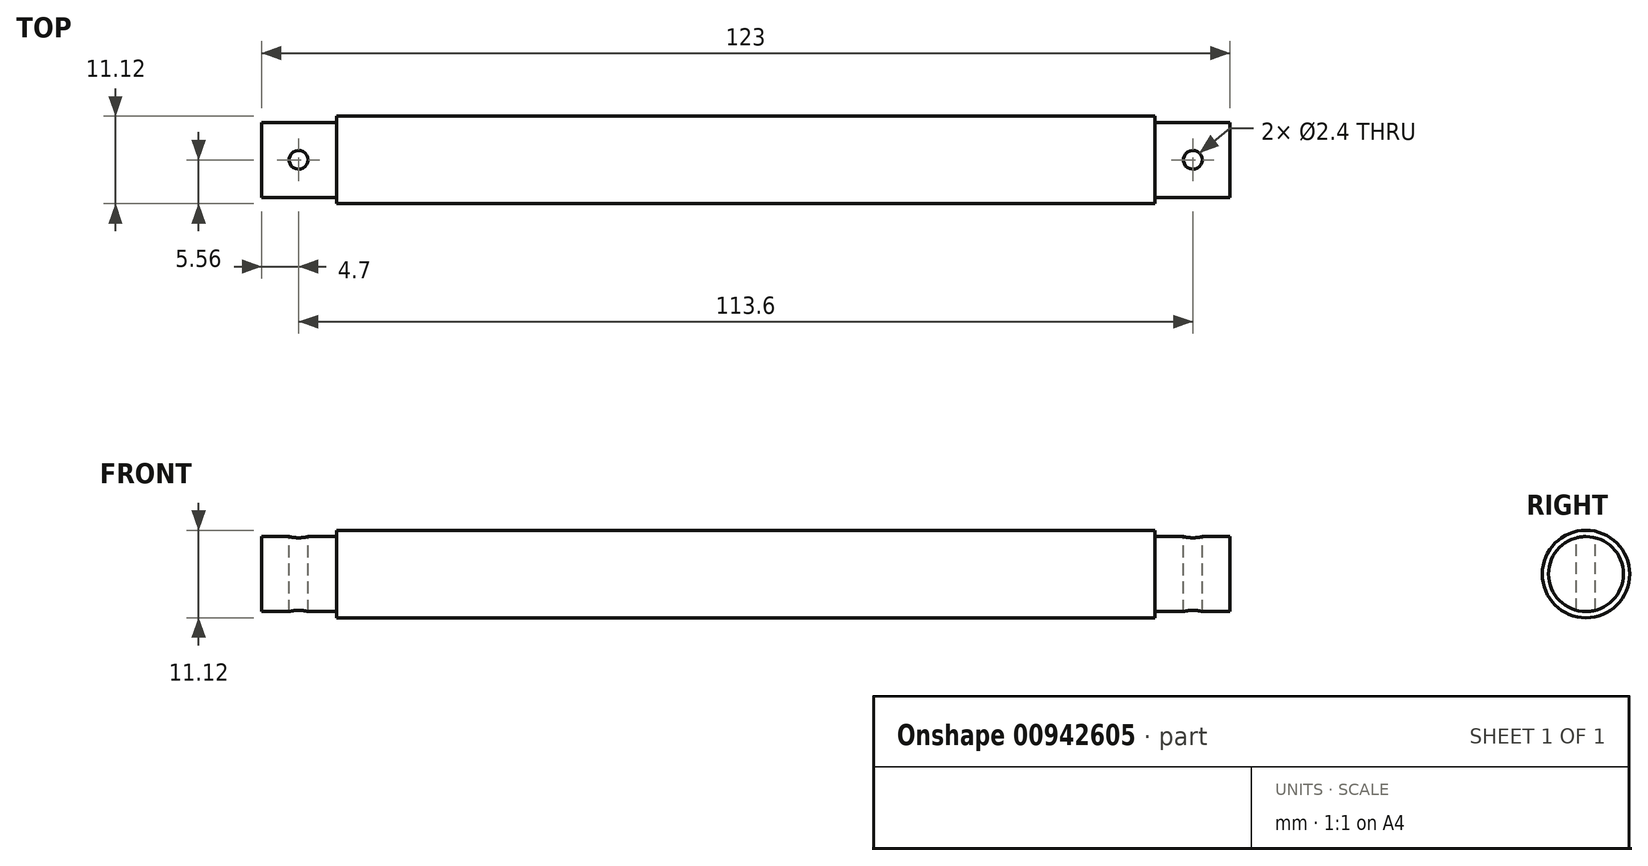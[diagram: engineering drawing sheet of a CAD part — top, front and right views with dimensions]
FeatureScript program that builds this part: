
annotation { "Feature Type Name" : "Feature", "Feature Type Description" : "" }
export const myFeature = defineFeature(function(context is Context, id is Id, definition is map)
    precondition{}
    {
        {
            var Q0;
            Q0=qCreatedBy(makeId("Right.planeOp"),FACE);
            var sketch = newSketch(context, id + "F0", { "sketchPlane" : qUnion([Q0])});
            skCircle(sketch, "E0", {"center": v(0, 0) * mm, "radius": 5.56 * mm});
            skSolve(sketch);
        }
        {
            var Q0;
            Q0 = qSketchRegion(id + "F0", true);
            extrude(context, id + "F1", {"entities" : qUnion([Q0]), "depth" : 52 * mm, "offsetDistance" : 25 * mm, "hasSecondDirection" : true, "secondDirectionOppositeDirection" : true, "secondDirectionDepth" : 52 * mm});
        }
        {
            var Q0;
            Q0=qCreatedBy(makeId("Right.planeOp"),FACE);
            var sketch = newSketch(context, id + "F2", { "sketchPlane" : qUnion([Q0])});
            skCircle(sketch, "E1", {"center": v(0, 0) * mm, "radius": 4.76 * mm});
            skSolve(sketch);
        }
        {
            var Q0;
            Q0 = qSketchRegion(id + "F2", true);
            extrude(context, id + "F3", {"entities" : qUnion([Q0]), "operationType" : NewBodyOperationType.ADD, "depth" : 61.5 * mm, "offsetDistance" : 25 * mm, "hasSecondDirection" : true, "secondDirectionOppositeDirection" : true, "secondDirectionDepth" : 61.5 * mm});
        }
        {
            var Q0;
            Q0=qCreatedBy(makeId("Top.planeOp"),FACE);
            var sketch = newSketch(context, id + "F4", { "sketchPlane" : qUnion([Q0])});
            skCircle(sketch, "E2", {"center": v(-56.8, 0) * mm, "radius": 1.2 * mm});
            skCircle(sketch, "E3", {"center": v(56.8, 0) * mm, "radius": 1.2 * mm});
            skSolve(sketch);
        }
        {
            var Q0;
            Q0 = qSketchRegion(id + "F4", true);
            extrude(context, id + "F5", {"entities" : qUnion([Q0]), "operationType" : NewBodyOperationType.REMOVE, "endBound" : BoundingType.THROUGH_ALL, "oppositeDirection" : true, "depth" : 25 * mm, "offsetDistance" : 25 * mm, "hasSecondDirection" : true, "secondDirectionBound" : SecondDirectionBoundingType.THROUGH_ALL, "secondDirectionOppositeDirection" : false, "secondDirectionDepth" : 25 * mm});
        }
    });
